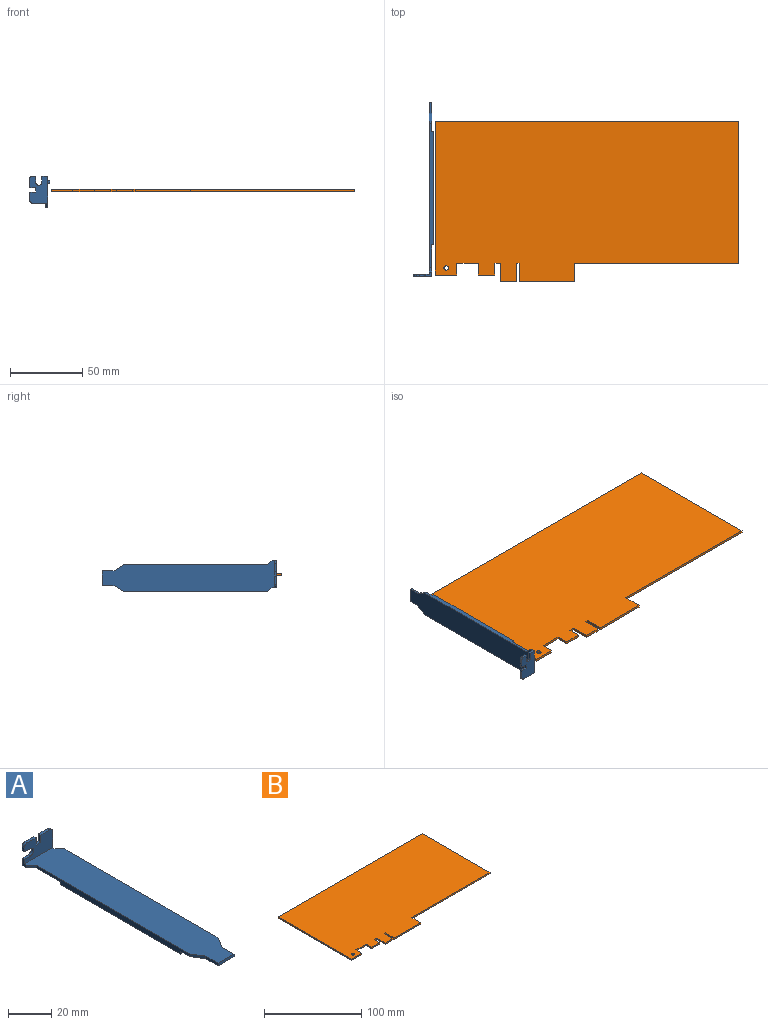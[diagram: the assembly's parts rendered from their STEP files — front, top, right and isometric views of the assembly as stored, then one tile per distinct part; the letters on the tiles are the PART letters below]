
ASSEMBLY  parts=2 mates=1
PART A: 30 faces, bbox 21.5x120.5x13.9 mm
  f0: plane 2.24x1.5mm, normal (-1,0,0), area 3.4mm2, adj f2,f3,f22,f24
  f1: plane 10.5x3mm, normal (1,0,0), area 18mm2, adj f2,f3,f15,f16,f17,f21
  f2: plane 18.5x12.4mm, normal (0,1,0), area 191.6mm2, adj f0,f1,f4,f5,f6,f17,f18,f19
  f3: plane 18.5x10.9mm, normal (0,-1,0), area 163.8mm2, adj f0,f1,f4,f5,f6,f16,f18,f19
  f4: plane 5.83x1.5mm, normal (0,0,1), area 8.7mm2, adj f2,f3,f20,f21
  f5: plane 5.83x1.5mm, normal (0,0,1), area 8.7mm2, adj f2,f3,f19,f22
  f6: plane 4x3mm, normal (-1,0,0), area 8.3mm2, adj f2,f3,f7,f16,f17,f23
  f7: plane 3.1x3.1mm, normal (-0.71,-0.71,0), area 6.6mm2, adj f6,f8,f16,f17
  f8: plane 99.9x3mm, normal (-1,0,0), area 267.4mm2, adj f7,f9,f16,f17,f26,f28,f29
  f9: plane 6.5x4.05mm, normal (-0.85,-0.53,0), area 11.5mm2, adj f8,f10,f16,f17
  f10: plane 8x1.5mm, normal (-1,0,0), area 12mm2, adj f9,f11,f16,f17
  f11: plane 10.3x1.5mm, normal (0,-1,0), area 15.5mm2, adj f10,f12,f16,f17
  f12: plane 8x1.5mm, normal (1,0,0), area 12mm2, adj f11,f13,f16,f17
  f13: plane 6.5x4.05mm, normal (0.85,-0.53,0), area 11.5mm2, adj f12,f14,f16,f17
  f14: plane 100x1.5mm, normal (1,0,0), area 150mm2, adj f13,f15,f16,f17
  f15: plane 3x3mm, normal (0.71,0.71,0), area 6.4mm2, adj f1,f14,f16,f17
  f16: plane 119x21.5mm, normal (0,0,1), area 2098.9mm2, adj f1,f3,f6,f7,f8,f9,f10,f11
  f17: plane 120.5x21.5mm, normal (0,0,-1), area 2009.1mm2, adj f1,f2,f6,f7,f8,f9,f10,f11
  f18: plane 3.05x1.5mm, normal (0,0,1), area 4.6mm2, adj f2,f3,f19,f20
  f19: plane 4.1x1.5mm, normal (1,0,0), area 6.2mm2, adj f2,f3,f5,f18
  f20: plane 4.1x1.5mm, normal (-1,0,0), area 6.2mm2, adj f2,f3,f4,f18
  f21: cylinder r=1.9mm len=1.9mm, axis (0,1,0), area 4.5mm2, adj f1,f2,f3,f4
  f22: cylinder r=1.9mm len=1.9mm, axis (0,1,0), area 4.5mm2, adj f0,f2,f3,f5
  f23: plane 3.91x1.5mm, normal (0,0,1), area 5.9mm2, adj f2,f3,f6,f25
  f24: plane 3.91x1.5mm, normal (0,0,-1), area 5.9mm2, adj f0,f2,f3,f25
  f25: cylinder r=2.13mm len=4.26mm, axis (0,1,0), area 10mm2, adj f2,f3,f23,f24
  f26: plane 1.5x1.5mm, normal (0,1,0), area 2.3mm2, adj f8,f17,f27,f29
  f27: plane 78.4x1.5mm, normal (1,0,0), area 117.6mm2, adj f17,f26,f28,f29
  f28: plane 1.5x1.5mm, normal (0,-1,0), area 2.3mm2, adj f8,f17,f27,f29
  f29: plane 78.4x1.5mm, normal (0,0,-1), area 117.6mm2, adj f8,f26,f27,f28
PART B: 21 faces, bbox 210x111.2x1.6 mm
  f0: plane 106.65x1.6mm, normal (-1,0,0), area 170.6mm2, adj f1,f18,f19,f20
  f1: plane 15x1.6mm, normal (0,-1,0), area 24mm2, adj f0,f2,f19,f20
  f2: plane 8.25x1.6mm, normal (1,0,0), area 13.2mm2, adj f1,f3,f19,f20
  f3: plane 14.7x1.6mm, normal (0,-1,0), area 23.5mm2, adj f2,f4,f19,f20
  f4: plane 8.25x1.6mm, normal (-1,0,0), area 13.2mm2, adj f3,f5,f19,f20
  f5: plane 11.65x1.6mm, normal (0,-1,0), area 18.6mm2, adj f4,f6,f19,f20
  f6: plane 8.25x1.6mm, normal (1,0,0), area 13.2mm2, adj f5,f7,f19,f20
  f7: plane 3.65x1.6mm, normal (0,-1,0), area 5.8mm2, adj f6,f8,f19,f20
  f8: plane 12.75x1.6mm, normal (-1,0,0), area 20.4mm2, adj f7,f9,f19,f20
  f9: plane 11.2x1.6mm, normal (0,-1,0), area 17.9mm2, adj f8,f10,f19,f20
  f10: plane 12.77x1.6mm, normal (1,0,0), area 20.4mm2, adj f9,f11,f19,f20
  f11: plane 1.9x1.6mm, normal (0,-1,0), area 3mm2, adj f10,f12,f19,f20
  f12: plane 12.77x1.6mm, normal (-1,0,0), area 20.4mm2, adj f11,f13,f19,f20
  f13: plane 38.2x1.6mm, normal (0,-1,0), area 61.1mm2, adj f12,f14,f19,f20
  f14: plane 12.77x1.6mm, normal (1,0,0), area 20.4mm2, adj f13,f15,f19,f20
  f15: plane 113.7x1.6mm, normal (0,-1,0), area 181.9mm2, adj f14,f16,f19,f20
  f16: plane 98.38x1.6mm, normal (1,0,0), area 157.4mm2, adj f15,f18,f19,f20
  f17: cylinder r=1.5mm len=3mm, axis (0,0,-1), area 15.1mm2, adj f19,f20
  f18: plane 210x1.6mm, normal (0,1,0), area 336mm2, adj f0,f16,f19,f20
  f19: plane 210x111.15mm, normal (0,0,1), area 21504.3mm2, adj f0,f1,f2,f3,f4,f5,f6,f7
  f20: plane 210x111.15mm, normal (0,0,-1), area 21504.3mm2, adj f0,f1,f2,f3,f4,f5,f6,f7
PLACE A rot(axis=(0.71,0,-0.71),180deg) t=(-12.81,117.85,20.4)mm
PLACE B t=(-10.24,12.78,12.91)mm fixed
MATE parallel B.f19 <-> A.f27  axis (0,0,1) through (92.93,68.08,14.51)mm
